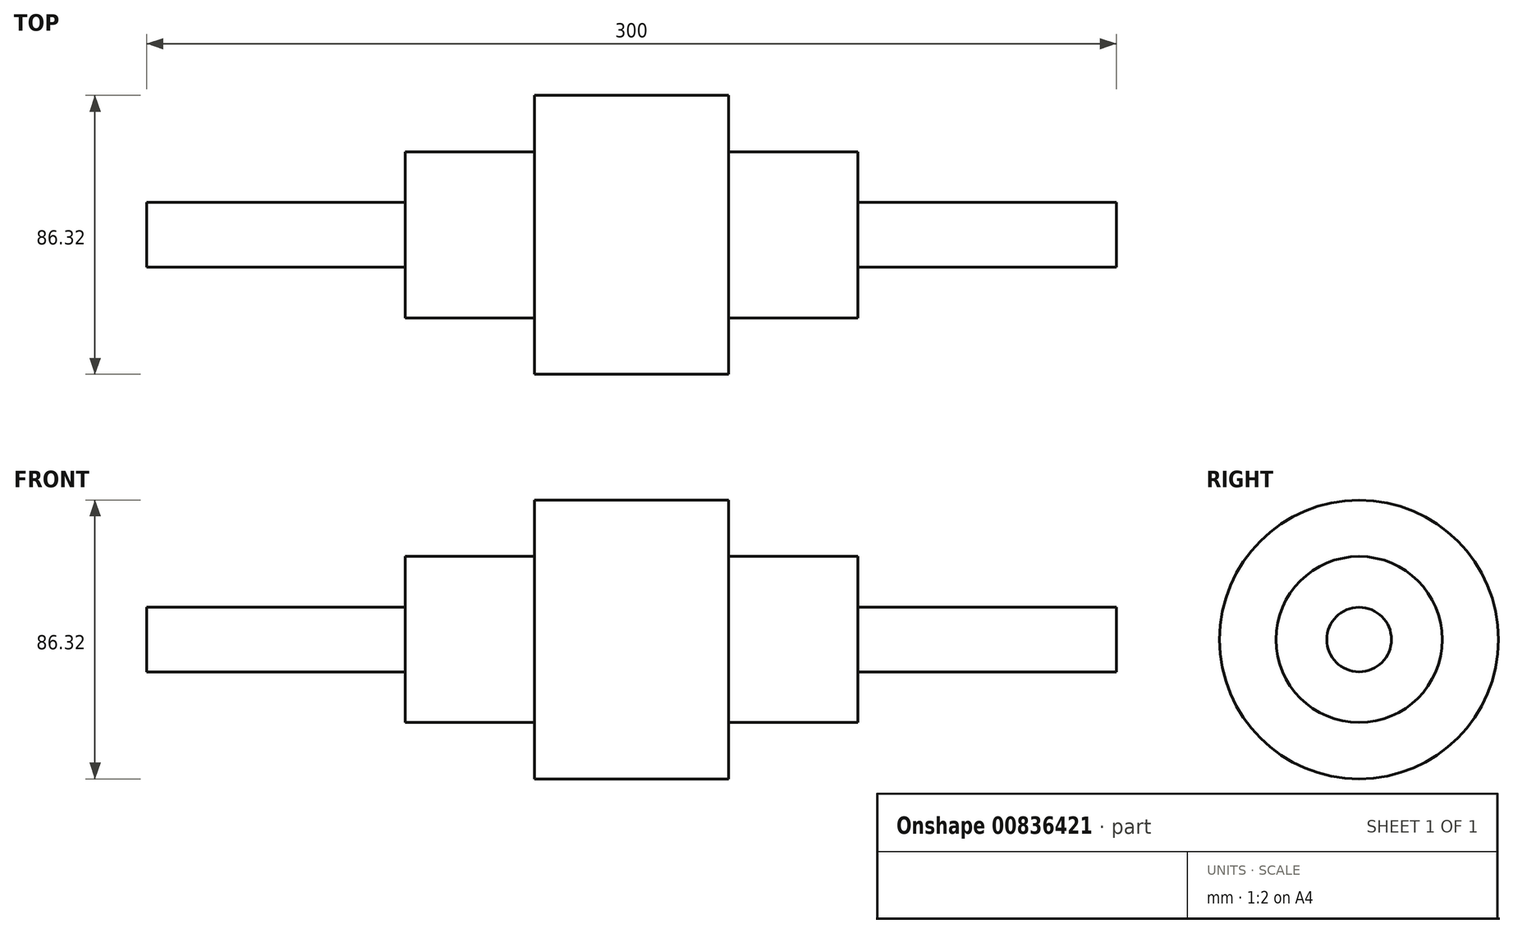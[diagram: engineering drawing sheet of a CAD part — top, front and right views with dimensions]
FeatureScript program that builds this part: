
annotation { "Feature Type Name" : "Feature", "Feature Type Description" : "" }
export const myFeature = defineFeature(function(context is Context, id is Id, definition is map)
    precondition{}
    {
        {
            var Q0;
            Q0=qCreatedBy(makeId("Top.planeOp"),FACE);
            var sketch = newSketch(context, id + "F0", { "sketchPlane" : qUnion([Q0])});
            skLineSegment(sketch, "E0", {"start": v(-150, 0) * mm, "end": v(-150, 10) * mm});
            skLineSegment(sketch, "E1", {"start": v(-150, 10) * mm, "end": v(-70, 10) * mm});
            skLineSegment(sketch, "E2", {"start": v(-70, 10) * mm, "end": v(-70, 25.72) * mm});
            skLineSegment(sketch, "E3", {"start": v(-70, 25.72) * mm, "end": v(-30, 25.72) * mm});
            skLineSegment(sketch, "E4", {"start": v(-30, 25.72) * mm, "end": v(-30, 43.16) * mm});
            skLineSegment(sketch, "E5", {"start": v(-30, 43.16) * mm, "end": v(30, 43.16) * mm});
            skLineSegment(sketch, "E6", {"start": v(30, 43.16) * mm, "end": v(30, 25.72) * mm});
            skLineSegment(sketch, "E7", {"start": v(30, 25.72) * mm, "end": v(70, 25.72) * mm});
            skLineSegment(sketch, "E8", {"start": v(70, 25.72) * mm, "end": v(70, 10) * mm});
            skLineSegment(sketch, "E9", {"start": v(70, 10) * mm, "end": v(150, 10) * mm});
            skLineSegment(sketch, "E10", {"start": v(150, 10) * mm, "end": v(150, 0) * mm});
            skLineSegment(sketch, "E11", {"start": v(150, 0) * mm, "end": v(-150, 0) * mm});
            skSolve(sketch);
        }
        {
            var Q0;
            Q0=makeQuery(id+"F0.imprint","IMPRINT",FACE,{"disambiguationData":[TD([[makeQuery(id+"F0.imprint","IMPRINT",EDGE,{"derivedFrom":sQuery(id+"F0.wireOp",EDGE,"E0")}),-1.0]])]});
            var Q1;
            Q1=sQuery(id+"F0.wireOp",EDGE,"E11");
            revolve(context, id + "F1", {"surfaceOperationType" : NewSurfaceOperationType.NEW, "entities" : qUnion([Q0]), "axis" : qUnion([Q1]), "revolveType" : RevolveType.FULL});
        }
    });
